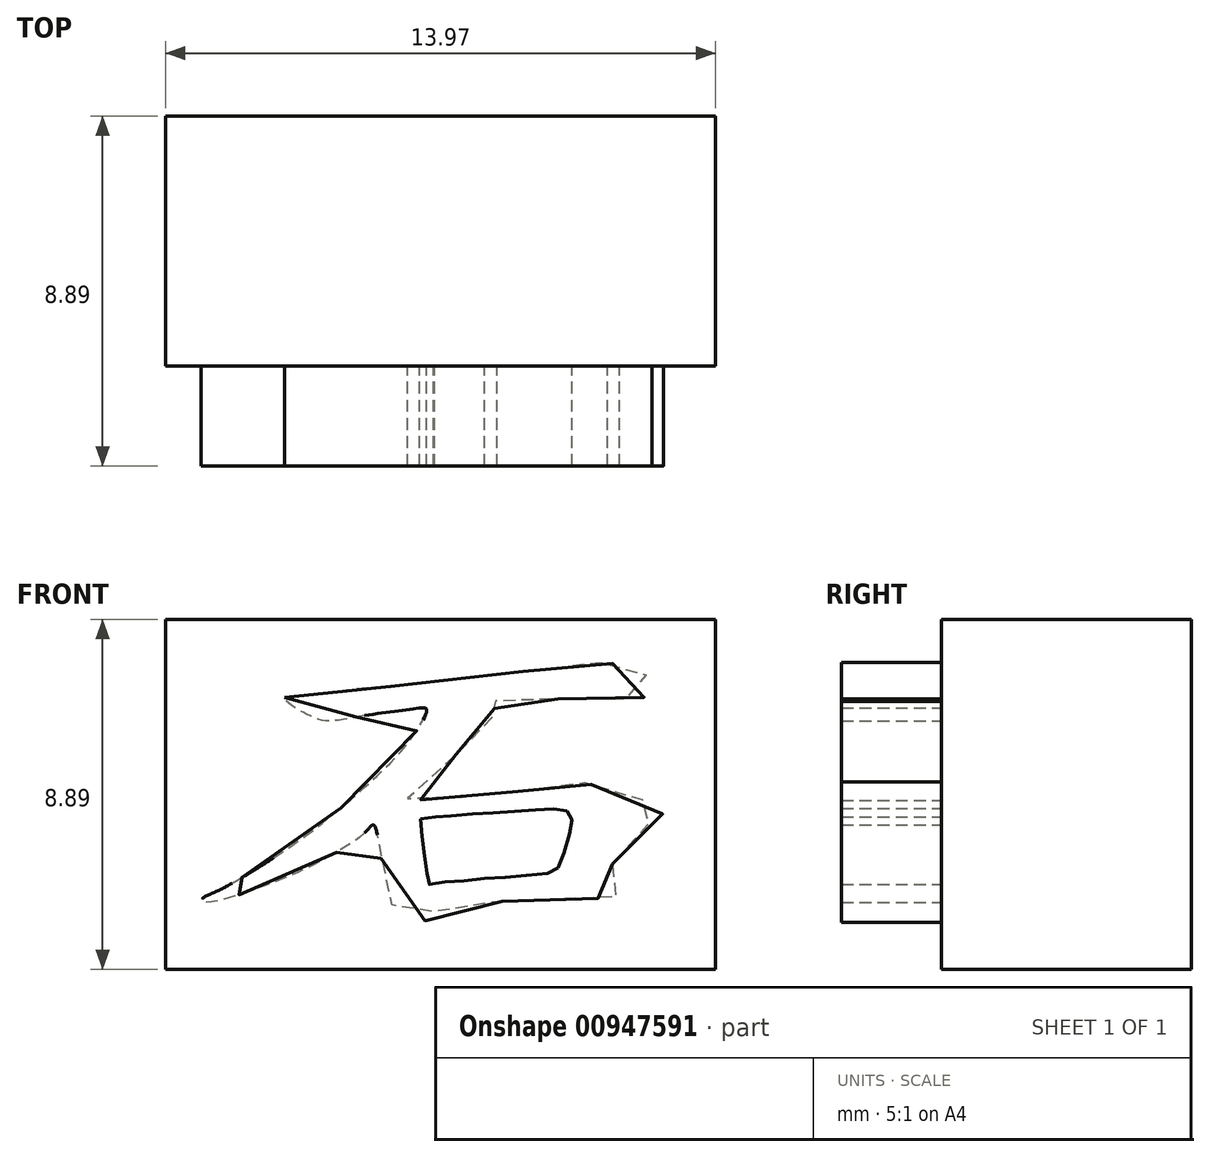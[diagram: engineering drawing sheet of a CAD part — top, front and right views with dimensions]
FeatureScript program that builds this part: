
annotation { "Feature Type Name" : "Feature", "Feature Type Description" : "" }
export const myFeature = defineFeature(function(context is Context, id is Id, definition is map)
    precondition{}
    {
        {
            var Q0;
            Q0=qCreatedBy(makeId("Front.planeOp"),FACE);
            var sketch = newSketch(context, id + "F0", { "sketchPlane" : qUnion([Q0])});
            skLineSegment(sketch, "E0.bottom", {"start": v(0, 0) * mm, "end": v(-13.97, 0) * mm});
            skLineSegment(sketch, "E0.top", {"start": v(0, 8.9) * mm, "end": v(-13.97, 8.89) * mm});
            skLineSegment(sketch, "E0.left", {"start": v(0, 0) * mm, "end": v(0, 8.9) * mm});
            skLineSegment(sketch, "E0.right", {"start": v(-13.97, 0) * mm, "end": v(-13.97, 8.89) * mm});
            skSolve(sketch);
        }
        {
            var Q0;
            Q0=makeQuery(id+"F0.imprint","IMPRINT",FACE,{"disambiguationData":[TD([[makeQuery(id+"F0.imprint","IMPRINT",EDGE,{"derivedFrom":sQuery(id+"F0.wireOp",EDGE,"E0.bottom")}),-1.0]])]});
            var sketch = newSketch(context, id + "F1", { "sketchPlane" : qUnion([Q0])});
            skFitSpline(sketch, "E1", {"points": [v(-10.95, 6.91) * mm, v(-10.37, 7) * mm, v(-9.36, 7.11) * mm, v(-7.96, 7.21) * mm, v(-6.67, 7.37) * mm, v(-4.85, 7.57) * mm, v(-3.82, 7.7) * mm, v(-3.3, 7.79) * mm, v(-2.72, 7.79) * mm, v(-2.38, 7.7) * mm, v(-1.96, 7.59) * mm, v(-1.68, 7.4) * mm, v(-1.62, 7.1) * mm, v(-1.82, 6.91) * mm, v(-2.38, 6.87) * mm, v(-3.14, 6.87) * mm, v(-3.82, 6.87) * mm, v(-4.35, 6.85) * mm, v(-5.07, 6.81) * mm, v(-5.87, 6.78) * mm, v(-5.57, 6.6) * mm, v(-5.57, 6.51) * mm, v(-5.63, 6.41) * mm, v(-5.73, 6.37) * mm, v(-6.1, 6) * mm, v(-6.5, 5.54) * mm, v(-7, 5.06) * mm, v(-7.48, 4.62) * mm, v(-7.82, 4.32) * mm, v(-7.36, 4.32) * mm, v(-6.7, 4.36) * mm, v(-5.85, 4.44) * mm, v(-4.87, 4.54) * mm, v(-4.17, 4.64) * mm, v(-3.64, 4.74) * mm, v(-3.42, 4.76) * mm, v(-3.16, 4.7) * mm, v(-2.54, 4.56) * mm, v(-1.78, 4.28) * mm, v(-1.32, 4.04) * mm, v(-1.36, 3.92) * mm, v(-1.6, 3.74) * mm, v(-1.92, 3.58) * mm, v(-2.34, 3.15) * mm, v(-2.62, 2.67) * mm, v(-2.74, 2.3) * mm, v(-2.54, 2.1) * mm, v(-2.44, 1.89) * mm, v(-2.62, 1.83) * mm, v(-2.96, 1.8) * mm, v(-3.62, 1.79) * mm, v(-4.45, 1.77) * mm, v(-5.35, 1.73) * mm, v(-6.35, 1.65) * mm, v(-7.16, 1.6) * mm, v(-7.14, 1.55) * mm, v(-7.32, 1.27) * mm, v(-7.74, 1.21) * mm, v(-8.14, 1.5) * mm, v(-8.42, 2.33) * mm, v(-8.56, 3.22) * mm, v(-8.69, 3.67) * mm, v(-8.88, 3.5) * mm, v(-9.42, 3.1) * mm, v(-10.15, 2.69) * mm, v(-11, 2.3) * mm, v(-12.07, 1.9) * mm, v(-12.98, 1.71) * mm, v(-13.06, 1.77) * mm, v(-12.66, 1.99) * mm, v(-11.9, 2.4) * mm, v(-10.85, 3.09) * mm, v(-9.73, 3.92) * mm, v(-8.86, 4.68) * mm, v(-8.06, 5.46) * mm, v(-7.56, 6.11) * mm, v(-7.34, 6.61) * mm, v(-7.7, 6.61) * mm, v(-8.88, 6.45) * mm, v(-9.87, 6.31) * mm, v(-10.33, 6.45) * mm, v(-10.75, 6.7) * mm, v(-10.95, 6.91) * mm]});
            skFitSpline(sketch, "E2", {"points": [v(-7.5, 3.83) * mm, v(-7.44, 3.35) * mm, v(-7.38, 2.78) * mm, v(-7.32, 2.36) * mm, v(-7.29, 2.17) * mm, v(-6.98, 2.2) * mm, v(-6.48, 2.24) * mm, v(-5.83, 2.31) * mm, v(-5.2, 2.35) * mm, v(-4.5, 2.43) * mm, v(-4.07, 2.49) * mm, v(-3.98, 2.63) * mm, v(-3.8, 3.1) * mm, v(-3.67, 3.6) * mm, v(-3.65, 3.82) * mm, v(-3.71, 3.96) * mm, v(-3.9, 4.08) * mm, v(-4.26, 4.06) * mm, v(-4.84, 4.04) * mm, v(-5.52, 3.98) * mm, v(-6.16, 3.95) * mm, v(-6.84, 3.89) * mm, v(-7.16, 3.88) * mm, v(-7.5, 3.83) * mm]});
            skSolve(sketch);
        }
        {
            var Q0;
            Q0=makeQuery(id+"F0.imprint","IMPRINT",FACE,{"disambiguationData":[TD([[makeQuery(id+"F0.imprint","IMPRINT",EDGE,{"derivedFrom":sQuery(id+"F0.wireOp",EDGE,"E0.bottom")}),-1.0]])]});
            extrude(context, id + "F2", {"entities" : qUnion([Q0]), "oppositeDirection" : true, "depth" : 6.35 * mm, "offsetDistance" : 25.4 * mm});
        }
        {
            var Q0;
            Q0=makeQuery(id+"F1.imprint","IMPRINT",FACE,{"disambiguationData":[TD([[makeQuery(id+"F1.imprint","IMPRINT",EDGE,{"derivedFrom":sQuery(id+"F1.wireOp",EDGE,"E1")}),-1.0]])]});
            extrude(context, id + "F3", {"entities" : qUnion([Q0]), "operationType" : NewBodyOperationType.ADD, "depth" : 2.54 * mm, "offsetDistance" : 25.4 * mm});
        }
    });
